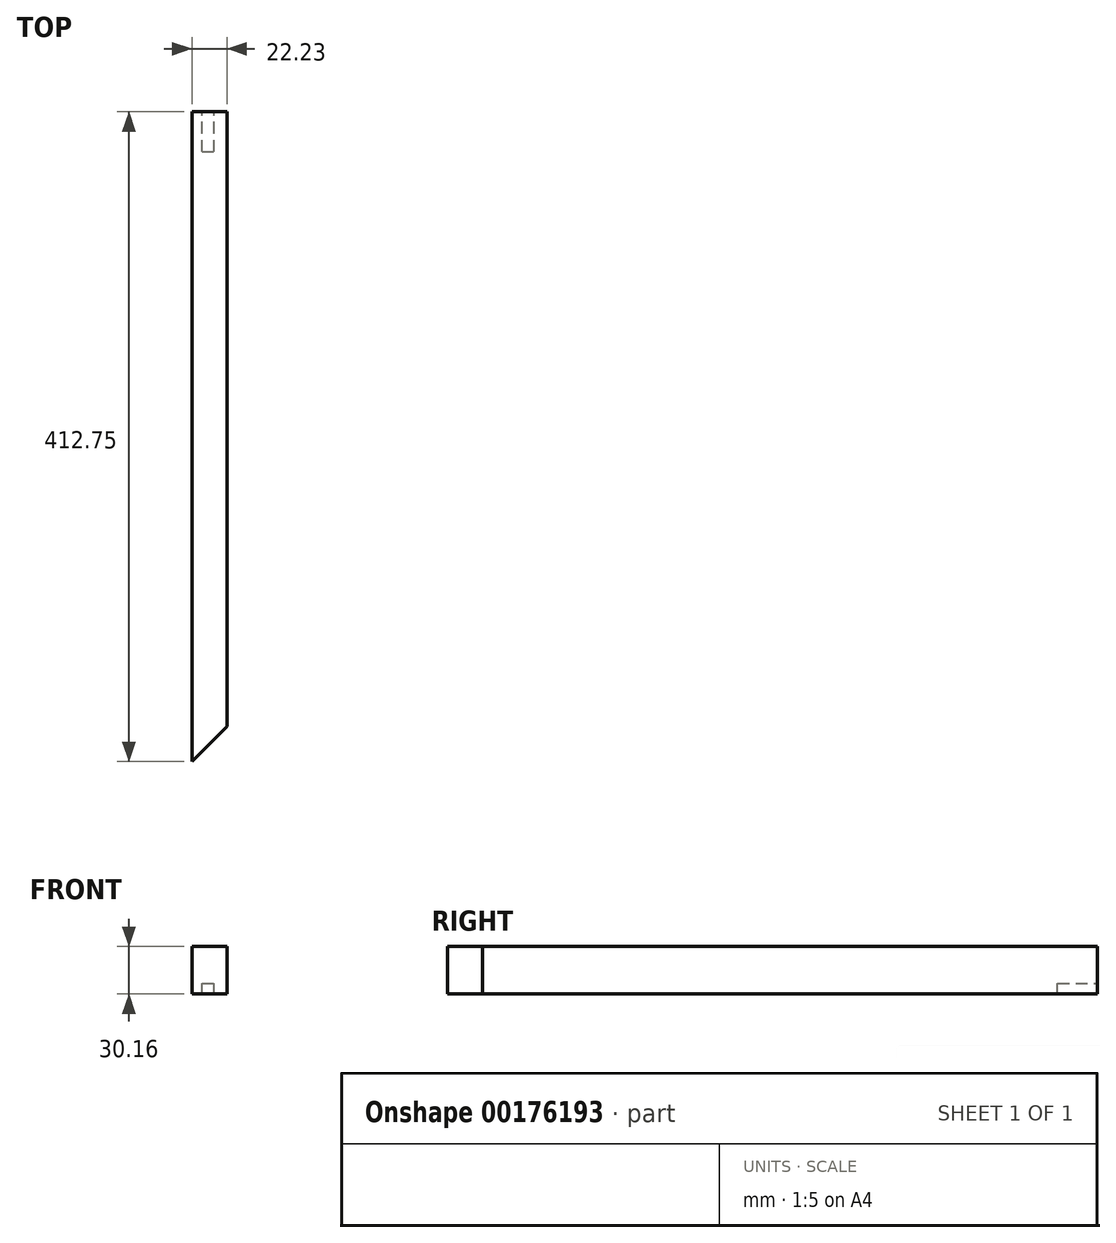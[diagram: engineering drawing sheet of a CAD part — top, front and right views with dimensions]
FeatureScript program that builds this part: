
annotation { "Feature Type Name" : "Feature", "Feature Type Description" : "" }
export const myFeature = defineFeature(function(context is Context, id is Id, definition is map)
    precondition{}
    {
        {
            var Q0;
            Q0=qCreatedBy(makeId("Top.planeOp"),FACE);
            var sketch = newSketch(context, id + "F0", { "sketchPlane" : qUnion([Q0])});
            skLineSegment(sketch, "E0.top", {"start": v(0, 412.75) * mm, "end": v(22.22, 412.75) * mm});
            skLineSegment(sketch, "E0.left", {"start": v(0, 0) * mm, "end": v(0, 412.75) * mm});
            skLineSegment(sketch, "E0.right", {"start": v(22.22, 22.22) * mm, "end": v(22.22, 412.75) * mm});
            skLineSegment(sketch, "E1", {"start": v(0, 0) * mm, "end": v(22.22, 22.22) * mm});
            skSolve(sketch);
        }
        {
            var Q0;
            Q0=makeQuery(id+"F0.imprint","IMPRINT",FACE,{"disambiguationData":[TD([[makeQuery(id+"F0.imprint","IMPRINT",EDGE,{"derivedFrom":sQuery(id+"F0.wireOp",EDGE,"E0.top")}),-1.0]])]});
            extrude(context, id + "F1", {"entities" : qUnion([Q0]), "depth" : 30.16 * mm});
        }
        {
            var Q0;
            Q0=makeQuery(id+"F1.opExtrude","SWEPT_FACE",FACE,{"disambiguationData":[OSD([sQuery(id+"F0.wireOp",EDGE,"E0.top")])]});
            var sketch = newSketch(context, id + "F2", { "sketchPlane" : qUnion([Q0])});
            skLineSegment(sketch, "E2.bottom", {"start": v(-6.35, 0) * mm, "end": v(-14.03, 0) * mm});
            skLineSegment(sketch, "E2.top", {"start": v(-6.35, 6.64) * mm, "end": v(-14.03, 6.64) * mm});
            skLineSegment(sketch, "E2.left", {"start": v(-6.35, 0) * mm, "end": v(-6.35, 6.64) * mm});
            skLineSegment(sketch, "E2.right", {"start": v(-14.03, 0) * mm, "end": v(-14.03, 6.64) * mm});
            skSolve(sketch);
        }
        {
            var Q0;
            Q0=makeQuery(id+"F2.imprint","IMPRINT",FACE,{"disambiguationData":[TD([[makeQuery(id+"F2.imprint","IMPRINT",EDGE,{"derivedFrom":sQuery(id+"F2.wireOp",EDGE,"E2.bottom")}),-1.0]])]});
            extrude(context, id + "F3", {"entities" : qUnion([Q0]), "operationType" : NewBodyOperationType.REMOVE, "oppositeDirection" : true, "depth" : 25.4 * mm});
        }
    });
